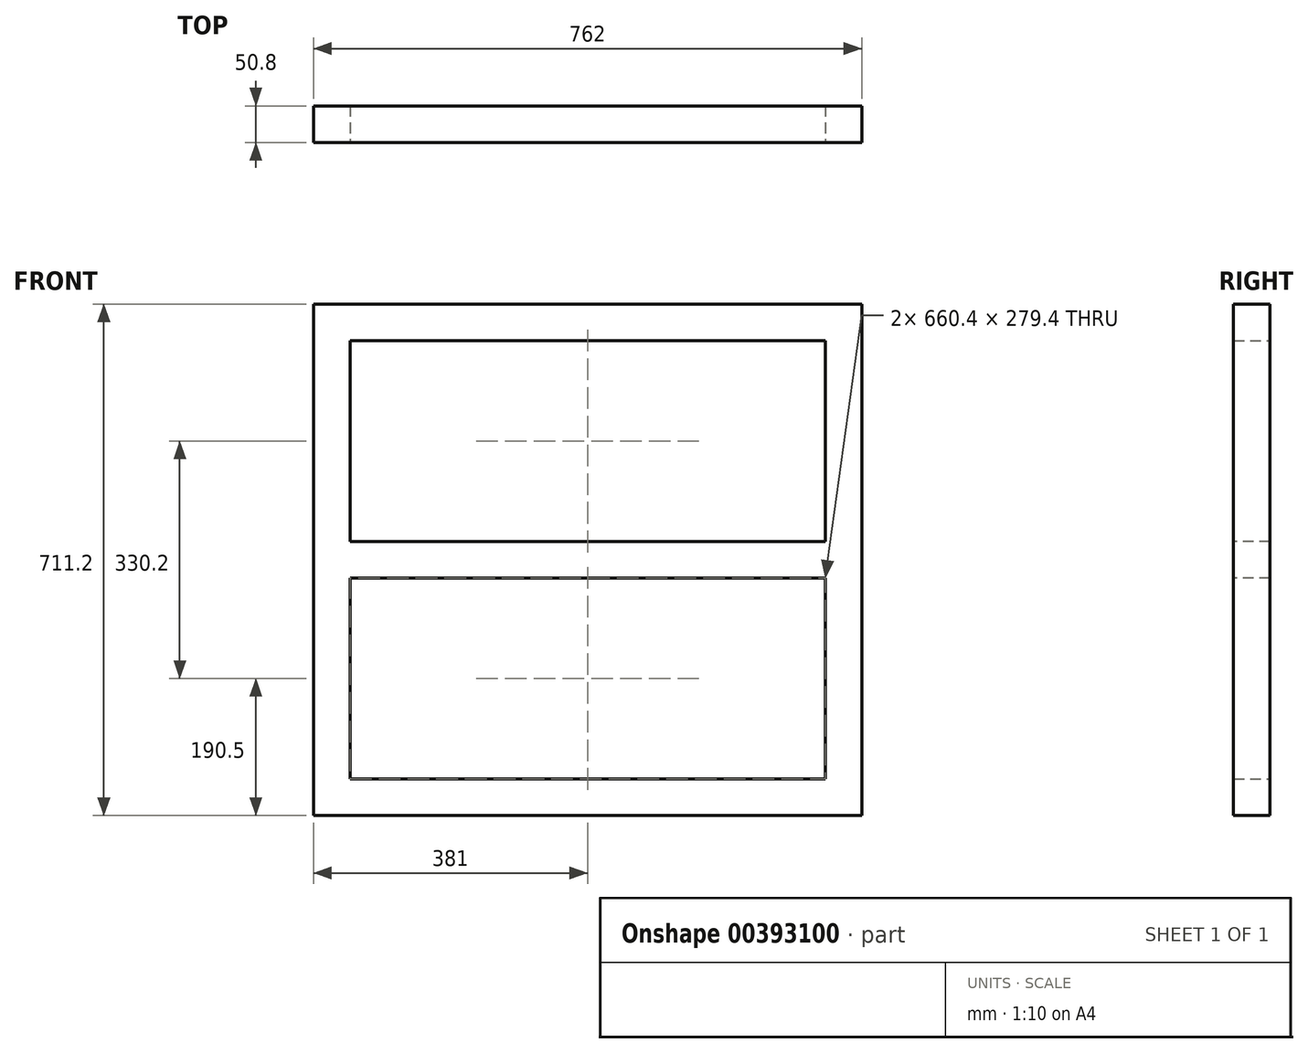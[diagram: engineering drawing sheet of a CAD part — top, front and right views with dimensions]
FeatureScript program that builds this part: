
annotation { "Feature Type Name" : "Feature", "Feature Type Description" : "" }
export const myFeature = defineFeature(function(context is Context, id is Id, definition is map)
    precondition{}
    {
        {
            var Q0;
            Q0=qCreatedBy(makeId("Front.planeOp"),FACE);
            var sketch = newSketch(context, id + "F0", { "sketchPlane" : qUnion([Q0])});
            skLineSegment(sketch, "E0.bottom", {"start": v(-381, 355.6) * mm, "end": v(381, 355.6) * mm, "construction": true});
            skLineSegment(sketch, "E0.top", {"start": v(-381, -355.6) * mm, "end": v(381, -355.6) * mm, "construction": true});
            skLineSegment(sketch, "E0.left", {"start": v(-381, 355.6) * mm, "end": v(-381, -355.6) * mm, "construction": true});
            skLineSegment(sketch, "E0.right", {"start": v(381, 355.6) * mm, "end": v(381, -355.6) * mm, "construction": true});
            skPoint(sketch, "E0.middle", {"position": v(0, 0) * mm});
            skLineSegment(sketch, "E1.bottom", {"start": v(-381, 355.6) * mm, "end": v(381, 355.6) * mm});
            skLineSegment(sketch, "E1.top", {"start": v(-381, -355.6) * mm, "end": v(381, -355.6) * mm});
            skLineSegment(sketch, "E1.left", {"start": v(-381, 355.6) * mm, "end": v(-381, -355.6) * mm});
            skLineSegment(sketch, "E1.right", {"start": v(381, 355.6) * mm, "end": v(381, -355.6) * mm});
            skLineSegment(sketch, "E2.bottom", {"start": v(-330.2, 304.8) * mm, "end": v(330.2, 304.8) * mm});
            skLineSegment(sketch, "E2.top", {"start": v(-330.2, -304.8) * mm, "end": v(330.2, -304.8) * mm});
            skLineSegment(sketch, "E2.left", {"start": v(-330.2, 304.8) * mm, "end": v(-330.2, -304.8) * mm});
            skLineSegment(sketch, "E2.right", {"start": v(330.2, 304.8) * mm, "end": v(330.2, -304.8) * mm});
            skSolve(sketch);
        }
        {
            var Q0;
            Q0 = qSketchRegion(id + "F0", true);
            extrude(context, id + "F1", {"entities" : qUnion([Q0]), "endBound" : BoundingType.SYMMETRIC, "depth" : 50.8 * mm});
        }
        {
            var Q0;
            Q0=qCreatedBy(makeId("Front.planeOp"),FACE);
            var sketch = newSketch(context, id + "F2", { "sketchPlane" : qUnion([Q0])});
            skLineSegment(sketch, "E3.left", {"start": v(-381, 0) * mm, "end": v(-381, -25.4) * mm});
            skLineSegment(sketch, "E3.right", {"start": v(381, 25.4) * mm, "end": v(381, 0) * mm});
            skPoint(sketch, "E3.middle", {"position": v(0, 0) * mm});
            skLineSegment(sketch, "E4.bottom", {"start": v(-381, -25.4) * mm, "end": v(381, -25.4) * mm});
            skLineSegment(sketch, "E4.top", {"start": v(-381, 25.4) * mm, "end": v(381, 25.4) * mm});
            skLineSegment(sketch, "E4.left", {"start": v(-381, -25.4) * mm, "end": v(-381, 25.4) * mm});
            skLineSegment(sketch, "E4.right", {"start": v(381, -25.4) * mm, "end": v(381, 25.4) * mm});
            skSolve(sketch);
        }
        {
            var Q0;
            Q0 = qSketchRegion(id + "F2", true);
            extrude(context, id + "F3", {"entities" : qUnion([Q0]), "operationType" : NewBodyOperationType.ADD, "endBound" : BoundingType.SYMMETRIC, "depth" : 50.8 * mm});
        }
    });
